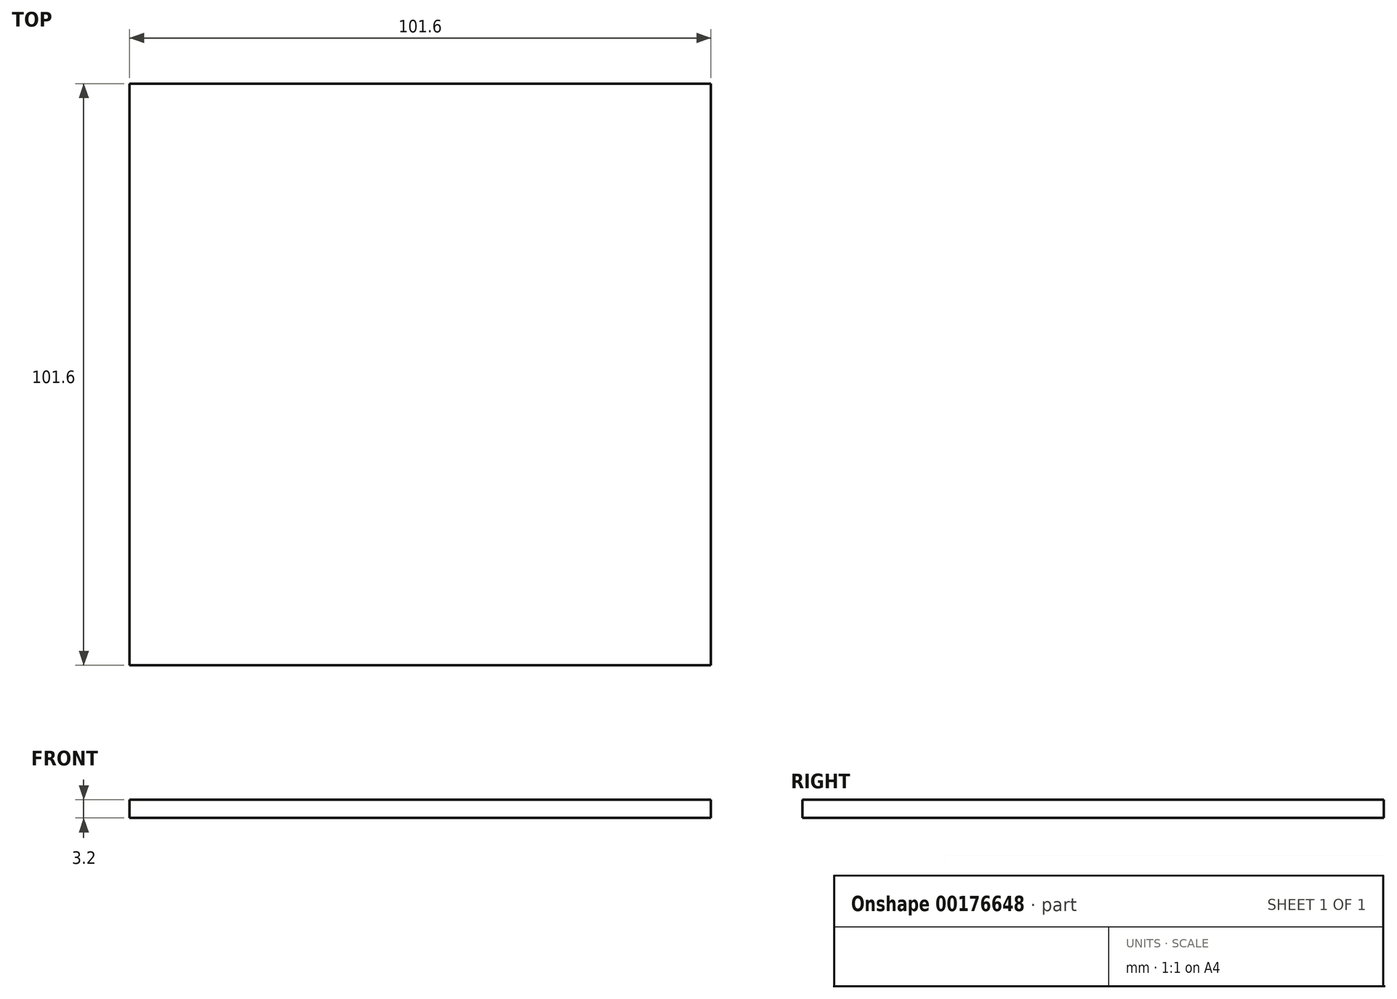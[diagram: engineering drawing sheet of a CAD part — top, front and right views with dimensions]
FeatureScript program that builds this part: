
annotation { "Feature Type Name" : "Feature", "Feature Type Description" : "" }
export const myFeature = defineFeature(function(context is Context, id is Id, definition is map)
    precondition{}
    {
        {
            var Q0;
            Q0=qCreatedBy(makeId("Top.planeOp"),FACE);
            var sketch = newSketch(context, id + "F0", { "sketchPlane" : qUnion([Q0])});
            skCircle(sketch, "E0", {"center": v(0, 0) * mm, "radius": 50.8 * mm, "construction": true});
            skLineSegment(sketch, "E1.bottom", {"start": v(50.8, 50.8) * mm, "end": v(-50.8, 50.8) * mm});
            skLineSegment(sketch, "E1.top", {"start": v(50.8, -50.8) * mm, "end": v(-50.8, -50.8) * mm});
            skLineSegment(sketch, "E1.left", {"start": v(50.8, 50.8) * mm, "end": v(50.8, -50.8) * mm});
            skLineSegment(sketch, "E1.right", {"start": v(-50.8, 50.8) * mm, "end": v(-50.8, -50.8) * mm});
            skSolve(sketch);
        }
        {
            var Q0;
            Q0 = qSketchRegion(id + "F0", true);
            extrude(context, id + "F1", {"entities" : qUnion([Q0]), "depth" : 3.2 * mm});
        }
    });
